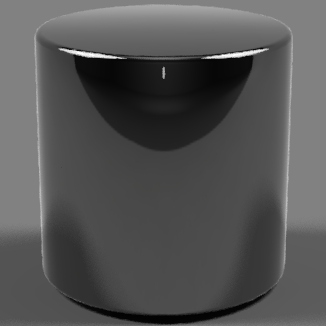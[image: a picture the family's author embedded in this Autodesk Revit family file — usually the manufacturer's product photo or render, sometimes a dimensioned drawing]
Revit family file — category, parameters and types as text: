
# Revit family: BLE-C-VDBW-E26
name_source: partatom
category: Lighting Fixtures
units: mm (PartAtom-declared; Revit-internal decimal feet)

## family parameters
Cut with Voids When Loaded = No
Host = Face
Light Source = Yes
Maintain Annotation Orientation = No
Part Type = Normal
Room Calculation Point = No
Round Connector Dimension = Use Diameter
Shared = No

## types (12) — shared parameters
Base Material = 100 - Black
Color Filter = 16777215
Cord Length = 3' - 0"
Cord Material = Rubber, Black
Default Elevation = 4' - 0"
Dimming Lamp Color Temperature Shift = <None>
Emit from Line Length = 2' - 0"
Head Height = 3' - 1 1/16"
Photometric Web File = generic
Shade Material = 100 - Black
Tilt Angle = -90.00°

## per-type parameters (varying)
| type | 10" VC | 10" VS | 12" VC | 12" VS | 14" VC | 14" VS | 16" VC | 16" VS | 20" VC | 20" VS | 24" VC | 24" VS | Heat Sink |
| 10" VC | Yes | No | No | No | No | No | No | No | No | No | No | No | 0' - 3 3/32" |
| 12" VC | No | No | Yes | No | No | No | No | No | No | No | No | No | 0' - 3 1/2" |
| 14" VC | No | No | No | No | Yes | No | No | No | No | No | No | No | 0' - 3 13/32" |
| 16" VC | No | No | No | No | No | No | Yes | No | No | No | No | No | 0' - 3 13/32" |
| 10" VS | No | Yes | No | No | No | No | No | No | No | No | No | No | 0' - 3 3/32" |
| 12" VS | No | No | No | Yes | No | No | No | No | No | No | No | No | 0' - 3 1/2" |
| 14" VS | No | No | No | No | No | Yes | No | No | No | No | No | No | 0' - 3 13/32" |
| 16" VS | No | No | No | No | No | No | No | Yes | No | No | No | No | 0' - 3 13/32" |
| 20" VC | No | No | No | No | No | No | No | No | Yes | No | No | No | 0' - 3 13/32" |
| 20" VS | No | No | No | No | No | No | No | No | No | Yes | No | No | 0' - 3 13/32" |
| 24" VC | No | No | No | No | No | No | No | No | No | No | Yes | No | 0' - 3 13/32" |
| 24" VS | No | No | No | No | No | No | No | No | No | No | No | Yes | 0' - 3 13/32" |

## geometry (parser evidence)
native form markers: Sweep x50
no freeform markers — native parametric forms only
